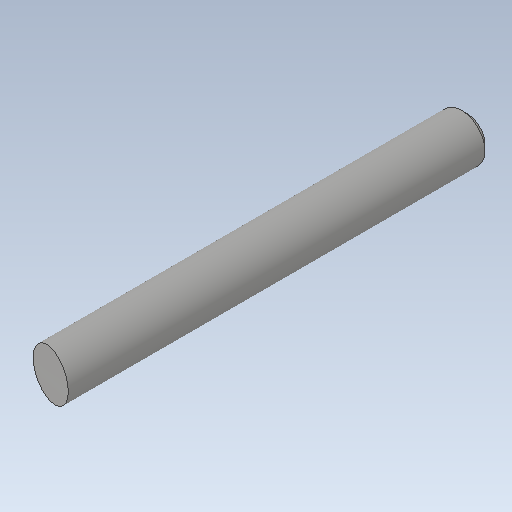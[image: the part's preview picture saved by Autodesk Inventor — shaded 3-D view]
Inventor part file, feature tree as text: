
AUTODESK INVENTOR PART (.ipt)
format: ipt  version: 2020.1 (Build 241239000, 239)  size: 130,048 bytes
history: native  units: mm
features: extrude x3, sketch x3, chamfer x1, projected_geometry x1
ambient origin geometry x8: Origin, YZ Plane, XZ Plane, XY Plane, X Axis, Y Axis, Z Axis, Center Point
bodies: Solid1 (feature_tree)
feature tree (8):
  extrude  "Extrusion1"  Depth=228.0mm
  extrude  "Extrusion2"  Depth=10.0mm TaperAngle=0.0deg
  extrude  "Extrusion3"  Depth=10.0mm
  chamfer  "Chamfer1"  Distance=10.0mm
  sketch  "Sketch1"  dims[d0=25.0mm d1=228.0mm]
  sketch  "Sketch2"  dims[d2=0.0mm d3=10.0mm d4=0.0mm]
  projected_geometry  "Projected Loop1"
  sketch  "Sketch3"  dims[d5=2.460914mm d6=2.953mm d7=10.0mm d8=0.0mm d9=3.0mm d10=2.0mm d11=45.0deg]
